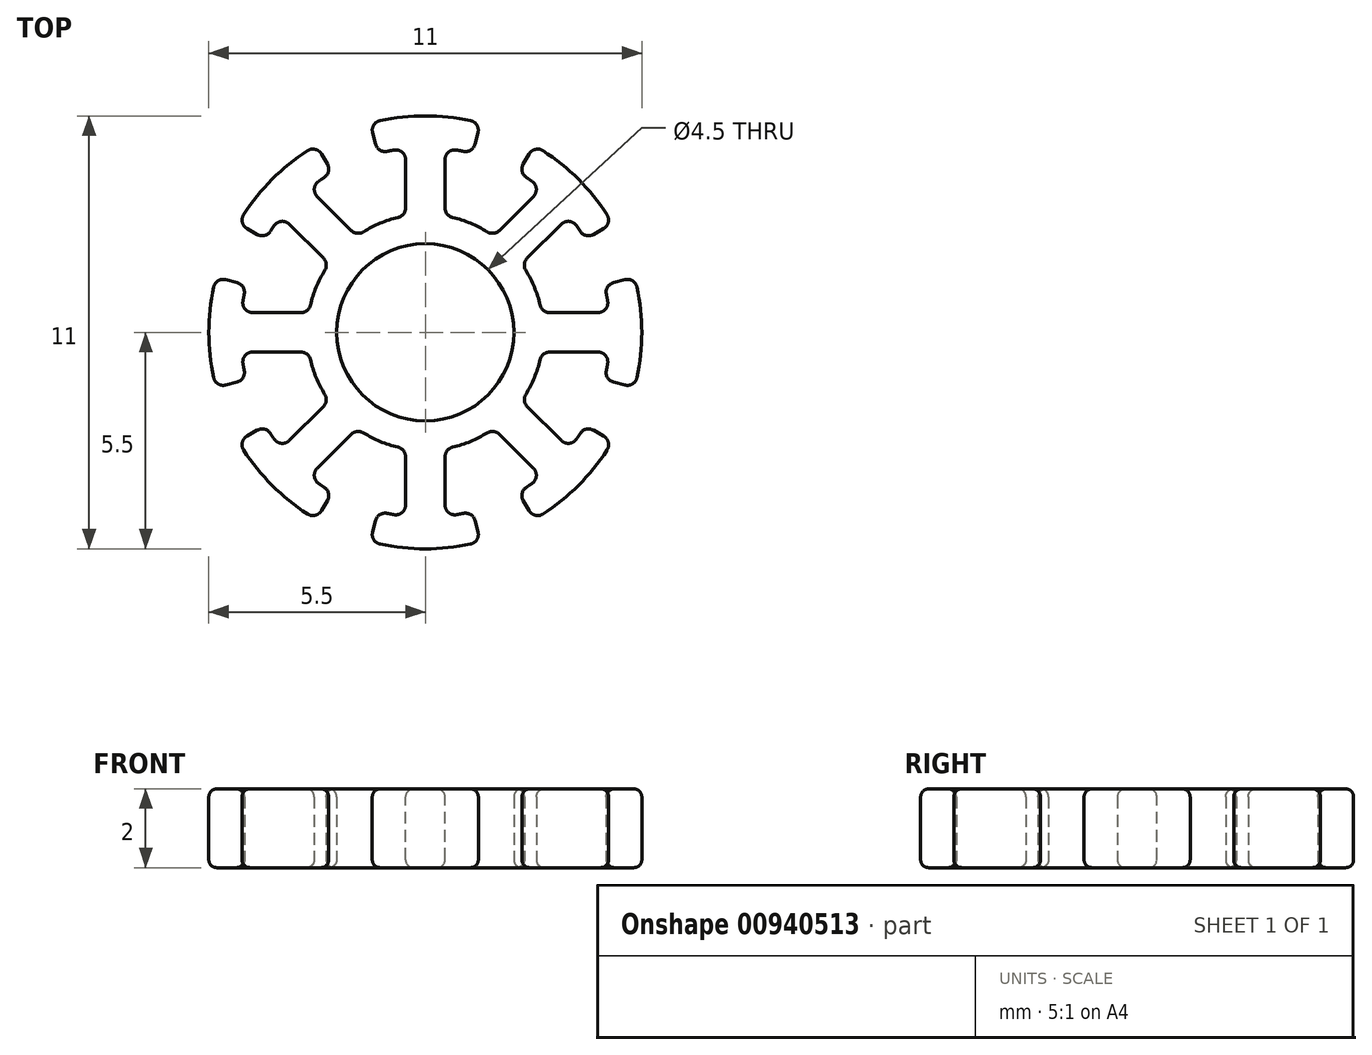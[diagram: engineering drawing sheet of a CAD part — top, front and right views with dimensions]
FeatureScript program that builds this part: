
annotation { "Feature Type Name" : "Feature", "Feature Type Description" : "" }
export const myFeature = defineFeature(function(context is Context, id is Id, definition is map)
    precondition{}
    {
        {
            var Q0;
            Q0=qCreatedBy(makeId("Top.planeOp"),FACE);
            var sketch = newSketch(context, id + "F0", { "sketchPlane" : qUnion([Q0])});
            skArc(sketch, "E0", {"start": v(1.4, 5.32) * mm, "mid": v(0, 5.5) * mm, "end": v(-1.4, 5.32) * mm});
            skCircle(sketch, "E1", {"center": v(0, 0) * mm, "radius": 2.25 * mm});
            skArc(sketch, "E2", {"start": v(-0.5, 4.67) * mm, "mid": v(-0.85, 4.62) * mm, "end": v(-1.2, 4.54) * mm});
            skLineSegment(sketch, "E3", {"start": v(-0.5, 2.96) * mm, "end": v(-0.5, 4.67) * mm});
            skCircle(sketch, "E4", {"center": v(0, 0) * mm, "radius": 3 * mm});
            skLineSegment(sketch, "E5.MirrorCS", {"start": v(0.5, 2.96) * mm, "end": v(0.5, 4.67) * mm});
            skLineSegment(sketch, "E6", {"start": v(-1.2, 4.54) * mm, "end": v(-1.4, 5.32) * mm});
            skLineSegment(sketch, "E7.MirrorCS", {"start": v(1.2, 4.54) * mm, "end": v(1.4, 5.32) * mm});
            skArc(sketch, "E8.MirrorCS", {"start": v(0.5, 4.67) * mm, "mid": v(0.85, 4.62) * mm, "end": v(1.2, 4.54) * mm});
            skSolve(sketch);
        }
        {
            var Q0;
            Q0 = qSketchRegion(id + "F0", true);
            extrude(context, id + "F1", {"entities" : qUnion([Q0]), "depth" : 2 * mm, "offsetDistance" : 25 * mm});
        }
        {
            var Q0;
            Q0=makeQuery(id+"F1.opExtrude","SWEPT_EDGE",EDGE,{"disambiguationData":[OSD([sQuery(id+"F0.wireOp",EDGE,"E2"),sQuery(id+"F0.wireOp",EDGE,"E3")])]});
            var Q1;
            Q1=makeQuery(id+"F1.opExtrude","SWEPT_EDGE",EDGE,{"disambiguationData":[OSD([sQuery(id+"F0.wireOp",EDGE,"E2"),sQuery(id+"F0.wireOp",EDGE,"E6")])]});
            var Q2;
            Q2=makeQuery(id+"F1.opExtrude","SWEPT_EDGE",EDGE,{"disambiguationData":[OSD([sQuery(id+"F0.wireOp",EDGE,"E0"),sQuery(id+"F0.wireOp",EDGE,"E6")])]});
            var Q3;
            Q3=makeQuery(id+"F1.opExtrude","SWEPT_EDGE",EDGE,{"disambiguationData":[OSD([sQuery(id+"F0.wireOp",EDGE,"E5.MirrorCS"),sQuery(id+"F0.wireOp",EDGE,"E8.MirrorCS")])]});
            var Q4;
            Q4=makeQuery(id+"F1.opExtrude","SWEPT_EDGE",EDGE,{"disambiguationData":[OSD([sQuery(id+"F0.wireOp",EDGE,"E7.MirrorCS"),sQuery(id+"F0.wireOp",EDGE,"E8.MirrorCS")])]});
            var Q5;
            Q5=makeQuery(id+"F1.opExtrude","SWEPT_EDGE",EDGE,{"disambiguationData":[OSD([sQuery(id+"F0.wireOp",EDGE,"E0"),sQuery(id+"F0.wireOp",EDGE,"E7.MirrorCS")])]});
            var Q6;
            Q6=makeQuery(id+"F1.opExtrude","SWEPT_EDGE",EDGE,{"disambiguationData":[OSD([sQuery(id+"F0.wireOp",EDGE,"E3"),sQuery(id+"F0.wireOp",EDGE,"E4")])]});
            var Q7;
            Q7=makeQuery(id+"F1.opExtrude","SWEPT_EDGE",EDGE,{"disambiguationData":[OSD([sQuery(id+"F0.wireOp",EDGE,"E4"),sQuery(id+"F0.wireOp",EDGE,"E5.MirrorCS")])]});
            fillet(context, id + "F2", {"entities" : qUnion([Q0, Q1, Q2, Q3, Q4, Q5, Q6, Q7]), "radius" : 0.25 * mm, "tangentPropagation" : true, "allowEdgeOverflow" : false});
        }
        {
            var Q0;
            Q0=makeQuery(id+"F1.opExtrude","CAP_FACE",FACE,{"disambiguationData":[OSD([sQuery(id+"F0.wireOp",EDGE,"E0"),sQuery(id+"F0.wireOp",EDGE,"E1"),sQuery(id+"F0.wireOp",EDGE,"E2"),sQuery(id+"F0.wireOp",EDGE,"E3"),sQuery(id+"F0.wireOp",EDGE,"E4"),sQuery(id+"F0.wireOp",EDGE,"E5.MirrorCS"),sQuery(id+"F0.wireOp",EDGE,"E6"),sQuery(id+"F0.wireOp",EDGE,"E7.MirrorCS"),sQuery(id+"F0.wireOp",EDGE,"E8.MirrorCS")])],"isStart":false});
            var Q1;
            Q1=makeQuery(id+"F1.opExtrude","CAP_FACE",FACE,{"disambiguationData":[OSD([sQuery(id+"F0.wireOp",EDGE,"E0"),sQuery(id+"F0.wireOp",EDGE,"E1"),sQuery(id+"F0.wireOp",EDGE,"E2"),sQuery(id+"F0.wireOp",EDGE,"E3"),sQuery(id+"F0.wireOp",EDGE,"E4"),sQuery(id+"F0.wireOp",EDGE,"E5.MirrorCS"),sQuery(id+"F0.wireOp",EDGE,"E6"),sQuery(id+"F0.wireOp",EDGE,"E7.MirrorCS"),sQuery(id+"F0.wireOp",EDGE,"E8.MirrorCS")])],"isStart":true});
            fillet(context, id + "F3", {"entities" : qUnion([Q0, Q1]), "radius" : 0.2 * mm, "tangentPropagation" : true, "allowEdgeOverflow" : false});
        }
        {
            var Q0;
            Q0=makeQuery(id+"F1.opExtrude","SWEPT_BODY",BODY,{"disambiguationData":[OSD([sQuery(id+"F0.wireOp",EDGE,"E0"),sQuery(id+"F0.wireOp",EDGE,"E1"),sQuery(id+"F0.wireOp",EDGE,"E2"),sQuery(id+"F0.wireOp",EDGE,"E3"),sQuery(id+"F0.wireOp",EDGE,"E4"),sQuery(id+"F0.wireOp",EDGE,"E5.MirrorCS"),sQuery(id+"F0.wireOp",EDGE,"E6"),sQuery(id+"F0.wireOp",EDGE,"E7.MirrorCS"),sQuery(id+"F0.wireOp",EDGE,"E8.MirrorCS")])]});
            var Q1;
            {var subQ0=sQuery(id+"F0.wireOp",EDGE,"E1");Q1=makeQuery(id+"F3.opFillet","BLEND_EDGE",EDGE,{"blendedFrom":[makeQuery(id+"F1.opExtrude","CAP_EDGE",EDGE,{"disambiguationData":[OSD([subQ0])],"isStart":false}),makeQuery(id+"F1.opExtrude","CAP_FACE",FACE,{"disambiguationData":[OSD([sQuery(id+"F0.wireOp",EDGE,"E0"),subQ0,sQuery(id+"F0.wireOp",EDGE,"E2"),sQuery(id+"F0.wireOp",EDGE,"E3"),sQuery(id+"F0.wireOp",EDGE,"E4"),sQuery(id+"F0.wireOp",EDGE,"E5.MirrorCS"),sQuery(id+"F0.wireOp",EDGE,"E6"),sQuery(id+"F0.wireOp",EDGE,"E7.MirrorCS"),sQuery(id+"F0.wireOp",EDGE,"E8.MirrorCS")])],"isStart":false})],"blendedInto":[makeQuery(id+"F1.opExtrude","CAP_FACE",FACE,{"disambiguationData":[OSD([sQuery(id+"F0.wireOp",EDGE,"E0"),subQ0,sQuery(id+"F0.wireOp",EDGE,"E2"),sQuery(id+"F0.wireOp",EDGE,"E3"),sQuery(id+"F0.wireOp",EDGE,"E4"),sQuery(id+"F0.wireOp",EDGE,"E5.MirrorCS"),sQuery(id+"F0.wireOp",EDGE,"E6"),sQuery(id+"F0.wireOp",EDGE,"E7.MirrorCS"),sQuery(id+"F0.wireOp",EDGE,"E8.MirrorCS")])],"isStart":false})]});}
            circularPattern(context, id + "F4", {"operationType" : NewBodyOperationType.ADD, "entities" : qUnion([Q0]), "axis" : qUnion([Q1]), "angle" : 360 * degree, "instanceCount" : 8, "equalSpace" : true});
        }
    });
